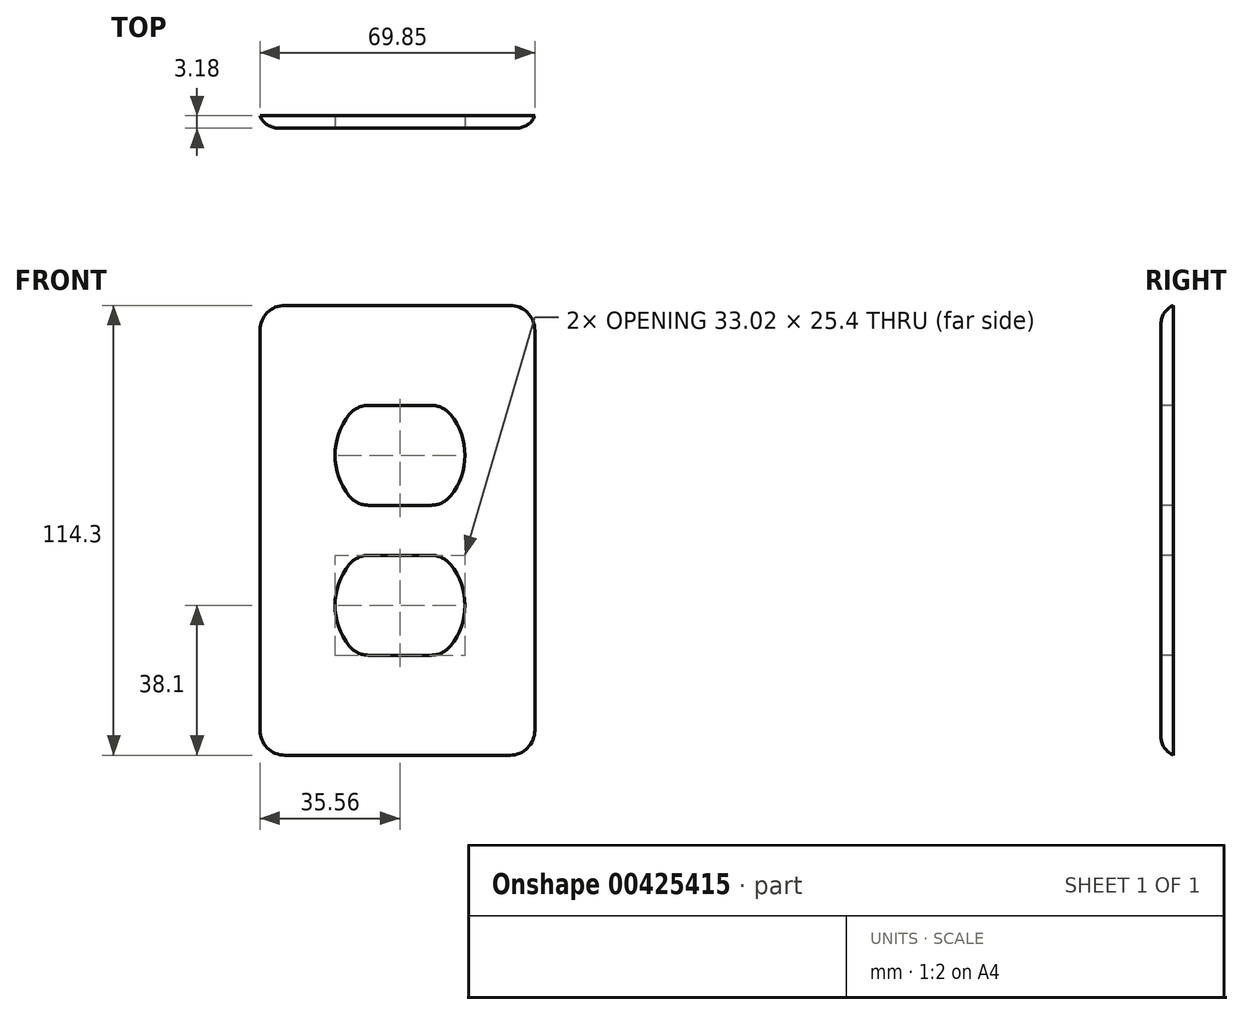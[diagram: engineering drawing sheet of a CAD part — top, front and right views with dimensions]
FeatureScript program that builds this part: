
annotation { "Feature Type Name" : "Feature", "Feature Type Description" : "" }
export const myFeature = defineFeature(function(context is Context, id is Id, definition is map)
    precondition{}
    {
        {
            var Q0;
            Q0=qCreatedBy(makeId("Front.planeOp"),FACE);
            var sketch = newSketch(context, id + "F0", { "sketchPlane" : qUnion([Q0])});
            skLineSegment(sketch, "E0.bottom", {"start": v(6.35, 0) * mm, "end": v(63.5, 0) * mm});
            skLineSegment(sketch, "E0.top", {"start": v(6.35, 114.3) * mm, "end": v(63.5, 114.3) * mm});
            skLineSegment(sketch, "E0.left", {"start": v(0, 6.35) * mm, "end": v(0, 107.95) * mm});
            skLineSegment(sketch, "E0.right", {"start": v(69.85, 6.35) * mm, "end": v(69.85, 107.95) * mm});
            skPoint(sketch, "E1.visualSharp", {"position": v(0, 114.3) * mm});
            skArc(sketch, "E1.filletArc", {"start": v(6.35, 114.3) * mm, "mid": v(1.86, 112.44) * mm, "end": v(0, 107.95) * mm});
            skPoint(sketch, "E2.visualSharp", {"position": v(69.85, 114.3) * mm});
            skArc(sketch, "E2.filletArc", {"start": v(69.85, 107.95) * mm, "mid": v(68, 112.44) * mm, "end": v(63.5, 114.3) * mm});
            skPoint(sketch, "E3.visualSharp", {"position": v(69.85, 0) * mm});
            skArc(sketch, "E3.filletArc", {"start": v(63.5, 0) * mm, "mid": v(68, 1.86) * mm, "end": v(69.85, 6.35) * mm});
            skPoint(sketch, "E4.visualSharp", {"position": v(0, 0) * mm});
            skArc(sketch, "E4.filletArc", {"start": v(0, 6.35) * mm, "mid": v(1.86, 1.86) * mm, "end": v(6.35, 0) * mm});
            skSolve(sketch);
        }
        {
            var Q0;
            Q0=makeQuery(id+"F0.imprint","IMPRINT",FACE,{"disambiguationData":[TD([[makeQuery(id+"F0.imprint","IMPRINT",EDGE,{"derivedFrom":sQuery(id+"F0.wireOp",EDGE,"E0.bottom")}),1.0]])]});
            extrude(context, id + "F1", {"entities" : qUnion([Q0]), "depth" : 3.17 * mm});
        }
        {
            var Q0;
            Q0=makeQuery(id+"F1.opExtrude","CAP_EDGE",EDGE,{"disambiguationData":[OSD([sQuery(id+"F0.wireOp",EDGE,"E0.top")])],"isStart":false});
            fillet(context, id + "F2", {"entities" : qUnion([Q0]), "radius" : 5.08 * mm, "tangentPropagation" : true, "allowEdgeOverflow" : false});
        }
        {
            var Q0;
            Q0=makeQuery(id+"F1.opExtrude","CAP_FACE",FACE,{"disambiguationData":[OSD([sQuery(id+"F0.wireOp",EDGE,"E0.bottom"),sQuery(id+"F0.wireOp",EDGE,"E0.top"),sQuery(id+"F0.wireOp",EDGE,"E0.left"),sQuery(id+"F0.wireOp",EDGE,"E0.right"),sQuery(id+"F0.wireOp",EDGE,"E1.filletArc"),sQuery(id+"F0.wireOp",EDGE,"E2.filletArc"),sQuery(id+"F0.wireOp",EDGE,"E3.filletArc"),sQuery(id+"F0.wireOp",EDGE,"E4.filletArc")])],"isStart":false});
            var sketch = newSketch(context, id + "F3", { "sketchPlane" : qUnion([Q0])});
            skArc(sketch, "E5", {"start": v(22.67, 86.52) * mm, "mid": v(19.05, 76.2) * mm, "end": v(22.67, 65.88) * mm});
            skLineSegment(sketch, "E6", {"start": v(27.63, 88.9) * mm, "end": v(43.5, 88.9) * mm});
            skLineSegment(sketch, "E7", {"start": v(27.63, 63.5) * mm, "end": v(43.5, 63.5) * mm});
            skArc(sketch, "E8.trimOffspring", {"start": v(48.45, 65.88) * mm, "mid": v(52.07, 76.2) * mm, "end": v(48.45, 86.52) * mm});
            skPoint(sketch, "E9.visualSharp", {"position": v(25.01, 88.9) * mm});
            skArc(sketch, "E9.filletArc", {"start": v(27.63, 88.9) * mm, "mid": v(24.88, 88.27) * mm, "end": v(22.67, 86.52) * mm});
            skPoint(sketch, "E10.visualSharp", {"position": v(46.1, 88.9) * mm});
            skArc(sketch, "E10.filletArc", {"start": v(48.45, 86.52) * mm, "mid": v(46.24, 88.27) * mm, "end": v(43.5, 88.9) * mm});
            skPoint(sketch, "E11.visualSharp", {"position": v(46.1, 63.5) * mm});
            skArc(sketch, "E11.filletArc", {"start": v(43.5, 63.5) * mm, "mid": v(46.24, 64.13) * mm, "end": v(48.45, 65.88) * mm});
            skPoint(sketch, "E12.visualSharp", {"position": v(25.01, 63.5) * mm});
            skArc(sketch, "E12.filletArc", {"start": v(22.67, 65.88) * mm, "mid": v(24.88, 64.13) * mm, "end": v(27.63, 63.5) * mm});
            skLineSegment(sketch, "E13.0", {"start": v(69.85, 6.35) * mm, "end": v(69.85, 107.95) * mm});
            skLineSegment(sketch, "E14", {"start": v(69.85, 57.15) * mm, "end": v(0, 57.15) * mm});
            skLineSegment(sketch, "E15.MirrorCS", {"start": v(27.63, 25.4) * mm, "end": v(43.5, 25.4) * mm});
            skLineSegment(sketch, "E16.MirrorCS", {"start": v(27.63, 50.8) * mm, "end": v(43.5, 50.8) * mm});
            skArc(sketch, "E17.MirrorCS", {"start": v(22.67, 27.78) * mm, "mid": v(19.05, 38.1) * mm, "end": v(22.67, 48.42) * mm});
            skArc(sketch, "E18.MirrorCS", {"start": v(48.45, 48.42) * mm, "mid": v(52.07, 38.1) * mm, "end": v(48.45, 27.78) * mm});
            skArc(sketch, "E19.MirrorCS", {"start": v(48.45, 27.78) * mm, "mid": v(46.24, 26.03) * mm, "end": v(43.5, 25.4) * mm});
            skArc(sketch, "E20.MirrorCS", {"start": v(27.63, 25.4) * mm, "mid": v(24.88, 26.03) * mm, "end": v(22.67, 27.78) * mm});
            skArc(sketch, "E21.MirrorCS", {"start": v(22.67, 48.42) * mm, "mid": v(24.88, 50.17) * mm, "end": v(27.63, 50.8) * mm});
            skArc(sketch, "E22.MirrorCS", {"start": v(43.5, 50.8) * mm, "mid": v(46.24, 50.17) * mm, "end": v(48.45, 48.42) * mm});
            skSolve(sketch);
        }
        {
            var Q0;
            Q0=makeQuery(id+"F3.imprint","IMPRINT",FACE,{"disambiguationData":[TD([[makeQuery(id+"F3.imprint","IMPRINT",EDGE,{"derivedFrom":sQuery(id+"F3.wireOp",EDGE,"E5")}),1.0]])]});
            var Q1;
            Q1=makeQuery(id+"F3.imprint","IMPRINT",FACE,{"disambiguationData":[TD([[makeQuery(id+"F3.imprint","IMPRINT",EDGE,{"derivedFrom":sQuery(id+"F3.wireOp",EDGE,"E15.MirrorCS")}),1.0]])]});
            extrude(context, id + "F4", {"entities" : qUnion([Q0, Q1]), "operationType" : NewBodyOperationType.REMOVE, "oppositeDirection" : true, "depth" : 25.4 * mm});
        }
    });
